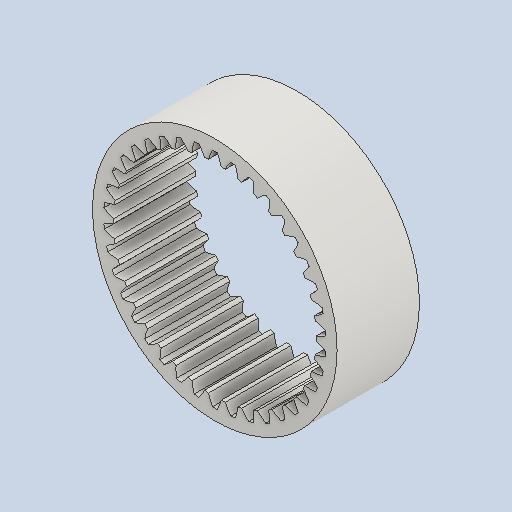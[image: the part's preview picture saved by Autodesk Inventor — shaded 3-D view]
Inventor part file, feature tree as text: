
AUTODESK INVENTOR PART (.ipt)
format: ipt  version: 2024 (Build 280153000, 153)  size: 324,608 bytes
history: native  units: mm (DEFAULTED — no unit token found)
features: plane x3, other x3, extrude x1, sketch x1
ambient origin geometry x8: Origin, YZ Plane, XZ Plane, XY Plane, X Axis, Y Axis, Z Axis, Center Point
bodies: Solid1 (feature_tree)
feature tree (8):
  extrude  "Extrusion1"  Depth=30.0mm TaperAngle=0.0deg
  plane  "Work Plane2"
  plane  "Work Plane8"
  plane  "Work Plane9"
  other  "Spur Gear"
  sketch  "Sketch1"  dims[d0=89.1mm d1=30.0mm d2=0.0mm d3=76.0mm d4=10.0mm d5=0.0mm d16=28.0mm d17=0.0mm d34=0.826735mm d39=0.0mm d45=0.0mm d47=28.0mm d50=0.0mm d51=0.0mm d52=28.0mm]
  other  "Srf1"
  other  "Pitch Diameter"
